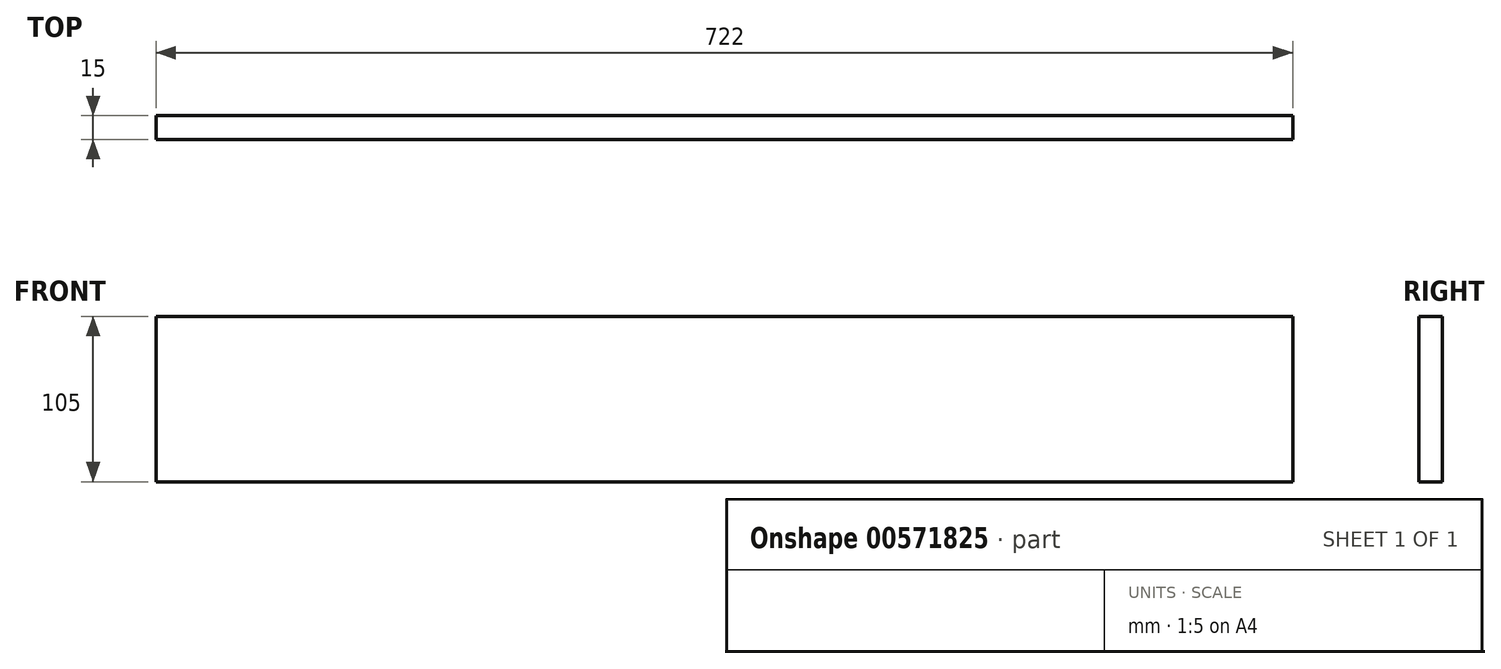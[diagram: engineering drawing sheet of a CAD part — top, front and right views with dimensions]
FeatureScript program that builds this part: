
annotation { "Feature Type Name" : "Feature", "Feature Type Description" : "" }
export const myFeature = defineFeature(function(context is Context, id is Id, definition is map)
    precondition{}
    {
        {
            var Q0;
            Q0=qCreatedBy(makeId("Front.planeOp"),FACE);
            var sketch = newSketch(context, id + "F0", { "sketchPlane" : qUnion([Q0])});
            skLineSegment(sketch, "E0.bottom", {"start": v(-359.6, 72.92) * mm, "end": v(362.4, 72.92) * mm});
            skLineSegment(sketch, "E0.top", {"start": v(-359.6, -32.08) * mm, "end": v(362.4, -32.08) * mm});
            skLineSegment(sketch, "E0.left", {"start": v(-359.6, 72.92) * mm, "end": v(-359.6, -32.08) * mm});
            skLineSegment(sketch, "E0.right", {"start": v(362.4, 72.92) * mm, "end": v(362.4, -32.08) * mm});
            skSolve(sketch);
        }
        {
            var Q0;
            Q0 = qSketchRegion(id + "F0", true);
            extrude(context, id + "F1", {"entities" : qUnion([Q0]), "depth" : 15 * mm, "offsetDistance" : 25 * mm});
        }
    });
